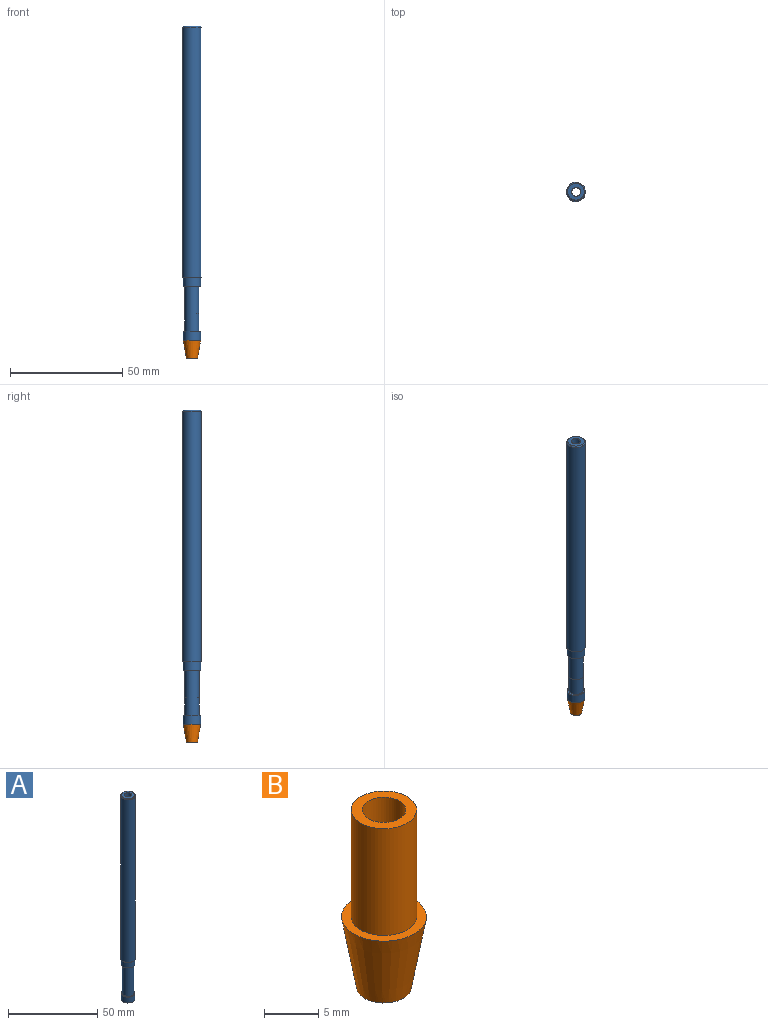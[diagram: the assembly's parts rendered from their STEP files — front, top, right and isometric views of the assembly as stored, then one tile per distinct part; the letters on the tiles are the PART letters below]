
ASSEMBLY  parts=2 mates=1
PART A: 13 faces, bbox 8.4x8.4x140 mm
  f0: cylinder r=2mm len=124.7mm, axis (0,0,-1), area 1567mm2, adj f1,f11
  f1: plane 7.4x7.4mm, normal (0,0,1), area 30.4mm2, adj f0,f10
  f2: cylinder r=4.2mm len=111.5mm, axis (0,0,-1), area 2942.4mm2, adj f3,f10
  f3: plane 8.4x8.4mm, normal (0,0,-1), area 7.6mm2, adj f2,f4
  f4: cylinder r=3.9mm len=7.8mm, axis (0,0,-1), area 98mm2, adj f3,f5
  f5: plane 7.8x7.8mm, normal (0,0,-1), area 17.1mm2, adj f4,f6
  f6: cylinder r=3.12mm len=20mm, axis (0,0,-1), area 392.7mm2, adj f5,f7
  f7: plane 7.8x7.8mm, normal (0,0,1), area 17.1mm2, adj f6,f8
  f8: cylinder r=3.9mm len=7.8mm, axis (0,0,-1), area 98mm2, adj f7,f9
  f9: plane 7.8x7.8mm, normal (0,0,-1), area 28.1mm2, adj f8,f12
  f10: cone r=4.2mm half-angle=45deg, axis (0,0,-1), area 17.5mm2, adj f1,f2
  f11: cone r=0mm half-angle=59deg, axis (0,0,-1), area 8.2mm2, adj f0,f12
  f12: cylinder r=2.5mm len=15mm, axis (0,0,-1), area 235.6mm2, adj f9,f11
PART B: 6 faces, bbox 7.8x7.8x19.9 mm
  f0: cylinder r=2mm len=19.94mm, axis (0,0,-1), area 250.6mm2, adj f1,f5
  f1: plane 6x6mm, normal (0,0,1), area 15.7mm2, adj f0,f2
  f2: cylinder r=3mm len=12mm, axis (0,0,-1), area 226.2mm2, adj f1,f3
  f3: plane 7.8x7.8mm, normal (0,0,1), area 19.5mm2, adj f2,f4
  f4: cone r=3.9mm half-angle=10deg, axis (0,0,1), area 162.1mm2, adj f3,f5
  f5: plane 5x5mm, normal (0,0,-1), area 7.1mm2, adj f0,f4
PLACE A t=(-22.14,-12,-4.83)mm
PLACE B t=(-22.14,-12,-4.83)mm
MATE fastened B.f0 <-> A.f0  axis (0,0,1) through (-22.14,-12,-4.83)mm
